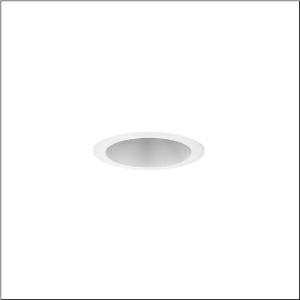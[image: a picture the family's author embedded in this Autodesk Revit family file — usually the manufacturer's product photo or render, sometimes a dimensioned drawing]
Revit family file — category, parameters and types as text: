
# Revit family: lunis_31_mini_51dn16de31
name_source: partatom
category: Lighting Fixtures
units: mm (PartAtom-declared; Revit-internal decimal feet)

## family parameters
Cut with Voids When Loaded = No
Host = Face
Light Source = No
Part Type = Normal
Room Calculation Point = No
Round Connector Dimension = Use Diameter
Shared = No

## types (1)
- Lunis 31 mini (1 x LED, 1000 lm, 8.3 W, 3000K)
    Apparent Load = 8 VA
    CIE Flux Codes = 69 93 99 100 100
    Color Rendering = 80
    Color Temperature = 3000K
    Default Elevation = 1800 mm
    Description = Lunis 31,  mini, downlight, light control with reflector, light emission: direct distribution, LED rated luminous flux: 1.000lm, light colour: 830, mains connection: 220..240V, AC, 50/60Hz, housing, white, protection rating (complete): IP20, protection rating (on room side): IP54, insulation class (complete): insulation class II (safety insulation), certification: CE, packaging unit: 1 piece
    Height = 0 mm  [stored 0 ft]
    Lamp = 1 x LED
    Lamp Light Flux = 1000 lm
    Lamp Power = 8.3 W
    Lamp count = 1
    Length = 188 mm  [stored 0.616798 ft]
    Luminous efficacy = 120 lm/W
    Manufacturer = Siteco
    ModVariant = No
    Model = 51DN16DE31
    Mounting Place = Ceiling
    Mounting Type = Recessed
    Number of Poles = 1
    OnlyDefault = Yes
    Power Factor = 1
    Product Name = Lunis 31 mini
    Product group = downlight
    ProductGroupID = 400
    Protection Class = Protection class II
    Protection Degree = IP 20
    RLX_Detail_Level = 1
    RLX_Emergency_Light_Flux = 0 lm
    RLX_Emergency_Type = 0
    RLX_Emergency_Type_DB = No
    RlxData = <blob elided: 21741 chars, md5=5e0b481f>
    Socket = socket
    Standby Power = 0 W
    System Light Flux = 1000 lm
    System Power = 8 W
    Type Comments = Product without accessories
    Type Image = l_1005624.jpg
    URL = http://relux.com
    VarID = ---
    Voltage = 0 V
    Weight = 0.00 kg
    Width = 0 mm  [stored 0 ft]

note: [stored X ft] marks values corroborated as IEEE doubles in the binary element streams (Revit-internal decimal feet)

## geometry (parser evidence)
native form markers: Blend x4, Sweep x12
no freeform markers — native parametric forms only
